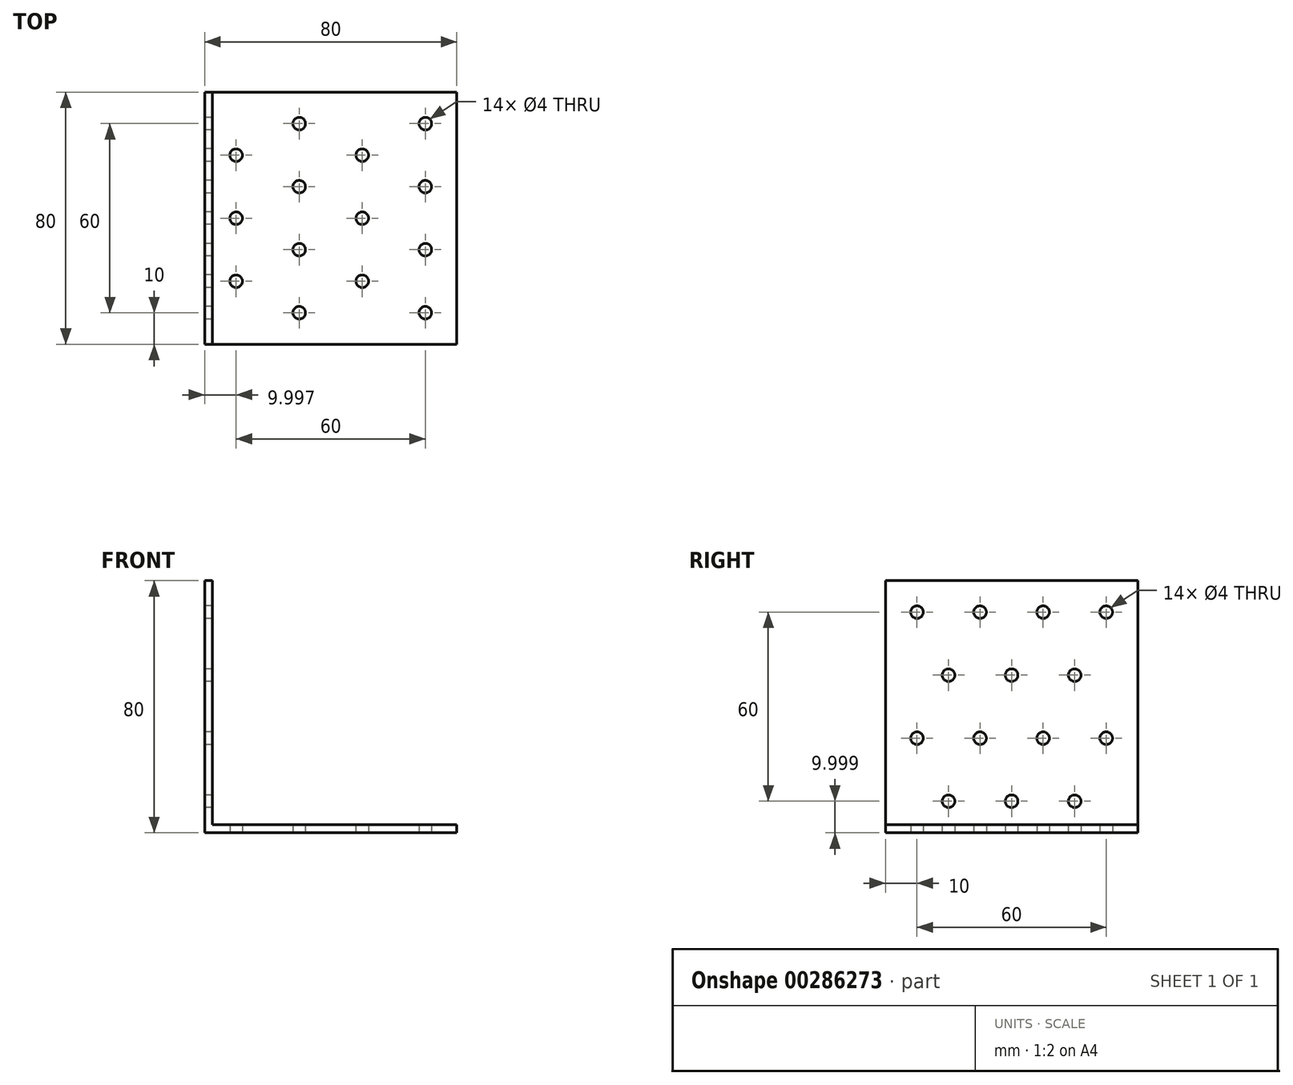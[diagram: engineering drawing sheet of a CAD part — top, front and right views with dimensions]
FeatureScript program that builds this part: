
annotation { "Feature Type Name" : "Feature", "Feature Type Description" : "" }
export const myFeature = defineFeature(function(context is Context, id is Id, definition is map)
    precondition{}
    {
        {
            var Q0;
            Q0=qCreatedBy(makeId("Front.planeOp"),FACE);
            var sketch = newSketch(context, id + "F0", { "sketchPlane" : qUnion([Q0])});
            skLineSegment(sketch, "E0.bottom", {"start": v(-46.27, 39.95) * mm, "end": v(-43.77, 39.95) * mm});
            skLineSegment(sketch, "E0.top", {"start": v(-46.27, -40.05) * mm, "end": v(-43.77, -40.05) * mm});
            skLineSegment(sketch, "E0.left", {"start": v(-46.27, 39.95) * mm, "end": v(-46.27, -40.05) * mm});
            skLineSegment(sketch, "E0.right", {"start": v(-43.77, 39.95) * mm, "end": v(-43.77, -37.55) * mm});
            skLineSegment(sketch, "E1.bottom", {"start": v(-46.27, -40.05) * mm, "end": v(33.73, -40.05) * mm});
            skLineSegment(sketch, "E1.top", {"start": v(-43.77, -37.55) * mm, "end": v(33.73, -37.55) * mm});
            skLineSegment(sketch, "E1.left", {"start": v(-46.27, -40.05) * mm, "end": v(-46.27, -37.55) * mm});
            skLineSegment(sketch, "E1.right", {"start": v(33.73, -40.05) * mm, "end": v(33.73, -37.55) * mm});
            skSolve(sketch);
        }
        {
            var Q0;
            Q0=makeQuery(id+"F0.imprint","IMPRINT",FACE,{"disambiguationData":[TD([[makeQuery(id+"F0.imprint","IMPRINT",EDGE,{"derivedFrom":sQuery(id+"F0.wireOp",EDGE,"E0.bottom")}),-1.0]])]});
            extrude(context, id + "F1", {"entities" : qUnion([Q0]), "depth" : 80 * mm});
        }
        {
            var Q0;
            Q0=makeQuery(id+"F1.opExtrude","SWEPT_FACE",FACE,{"disambiguationData":[OSD([sQuery(id+"F0.wireOp",EDGE,"E0.left"),sQuery(id+"F0.wireOp",EDGE,"E1.left")])]});
            var sketch = newSketch(context, id + "F2", { "sketchPlane" : qUnion([Q0])});
            skCircle(sketch, "E2", {"center": v(10, 29.95) * mm, "radius": 2 * mm});
            skCircle(sketch, "E3.0.1.0", {"center": v(10, -10.05) * mm, "radius": 2 * mm});
            skCircle(sketch, "E3.1.0.0", {"center": v(30, 29.95) * mm, "radius": 2 * mm});
            skCircle(sketch, "E3.1.1.0", {"center": v(30, -10.05) * mm, "radius": 2 * mm});
            skCircle(sketch, "E3.2.0.0", {"center": v(50, 29.95) * mm, "radius": 2 * mm});
            skCircle(sketch, "E3.2.1.0", {"center": v(50, -10.05) * mm, "radius": 2 * mm});
            skCircle(sketch, "E3.3.0.0", {"center": v(70, 29.95) * mm, "radius": 2 * mm});
            skCircle(sketch, "E3.3.1.0", {"center": v(70, -10.05) * mm, "radius": 2 * mm});
            skLineSegment(sketch, "E3.direction1", {"start": v(10, 29.95) * mm, "end": v(30, 29.95) * mm, "construction": true});
            skLineSegment(sketch, "E3.direction2", {"start": v(10, 29.95) * mm, "end": v(10, -10.05) * mm, "construction": true});
            skCircle(sketch, "E4", {"center": v(20, 9.95) * mm, "radius": 2 * mm});
            skCircle(sketch, "E5.0.1.0", {"center": v(20, -30.05) * mm, "radius": 2 * mm});
            skCircle(sketch, "E5.1.0.0", {"center": v(40, 9.95) * mm, "radius": 2 * mm});
            skCircle(sketch, "E5.1.1.0", {"center": v(40, -30.05) * mm, "radius": 2 * mm});
            skCircle(sketch, "E5.2.0.0", {"center": v(60, 9.95) * mm, "radius": 2 * mm});
            skCircle(sketch, "E5.2.1.0", {"center": v(60, -30.05) * mm, "radius": 2 * mm});
            skLineSegment(sketch, "E5.direction1", {"start": v(20, 9.95) * mm, "end": v(40, 9.95) * mm, "construction": true});
            skLineSegment(sketch, "E5.direction2", {"start": v(20, 9.95) * mm, "end": v(20, -30.05) * mm, "construction": true});
            skSolve(sketch);
        }
        {
            var Q0;
            Q0 = qSketchRegion(id + "F2", true);
            extrude(context, id + "F3", {"entities" : qUnion([Q0]), "operationType" : NewBodyOperationType.REMOVE, "oppositeDirection" : true, "depth" : 25 * mm});
        }
        {
            var Q0;
            Q0=makeQuery(id+"F1.opExtrude","SWEPT_FACE",FACE,{"disambiguationData":[OSD([sQuery(id+"F0.wireOp",EDGE,"E1.bottom")])]});
            var sketch = newSketch(context, id + "F4", { "sketchPlane" : qUnion([Q0])});
            skCircle(sketch, "E6", {"center": v(23.73, 70) * mm, "radius": 2 * mm});
            skCircle(sketch, "E7.0.1.0", {"center": v(23.73, 50) * mm, "radius": 2 * mm});
            skCircle(sketch, "E7.0.2.0", {"center": v(23.73, 30) * mm, "radius": 2 * mm});
            skCircle(sketch, "E7.0.3.0", {"center": v(23.73, 10) * mm, "radius": 2 * mm});
            skCircle(sketch, "E7.1.0.0", {"center": v(-16.27, 70) * mm, "radius": 2 * mm});
            skCircle(sketch, "E7.1.1.0", {"center": v(-16.27, 50) * mm, "radius": 2 * mm});
            skCircle(sketch, "E7.1.2.0", {"center": v(-16.27, 30) * mm, "radius": 2 * mm});
            skCircle(sketch, "E7.1.3.0", {"center": v(-16.27, 10) * mm, "radius": 2 * mm});
            skLineSegment(sketch, "E7.direction1", {"start": v(23.73, 70) * mm, "end": v(-16.27, 70) * mm, "construction": true});
            skLineSegment(sketch, "E7.direction2", {"start": v(23.73, 70) * mm, "end": v(23.73, 50) * mm, "construction": true});
            skCircle(sketch, "E8", {"center": v(3.73, 60) * mm, "radius": 2 * mm});
            skCircle(sketch, "E9.0.1.0", {"center": v(3.73, 40) * mm, "radius": 2 * mm});
            skCircle(sketch, "E9.0.2.0", {"center": v(3.73, 20) * mm, "radius": 2 * mm});
            skCircle(sketch, "E9.1.0.0", {"center": v(-36.27, 60) * mm, "radius": 2 * mm});
            skCircle(sketch, "E9.1.1.0", {"center": v(-36.27, 40) * mm, "radius": 2 * mm});
            skCircle(sketch, "E9.1.2.0", {"center": v(-36.27, 20) * mm, "radius": 2 * mm});
            skLineSegment(sketch, "E9.direction1", {"start": v(3.73, 60) * mm, "end": v(-36.27, 60) * mm, "construction": true});
            skLineSegment(sketch, "E9.direction2", {"start": v(3.73, 60) * mm, "end": v(3.73, 40) * mm, "construction": true});
            skSolve(sketch);
        }
        {
            var Q0;
            Q0 = qSketchRegion(id + "F4", true);
            extrude(context, id + "F5", {"entities" : qUnion([Q0]), "operationType" : NewBodyOperationType.REMOVE, "oppositeDirection" : true, "depth" : 25 * mm});
        }
    });
